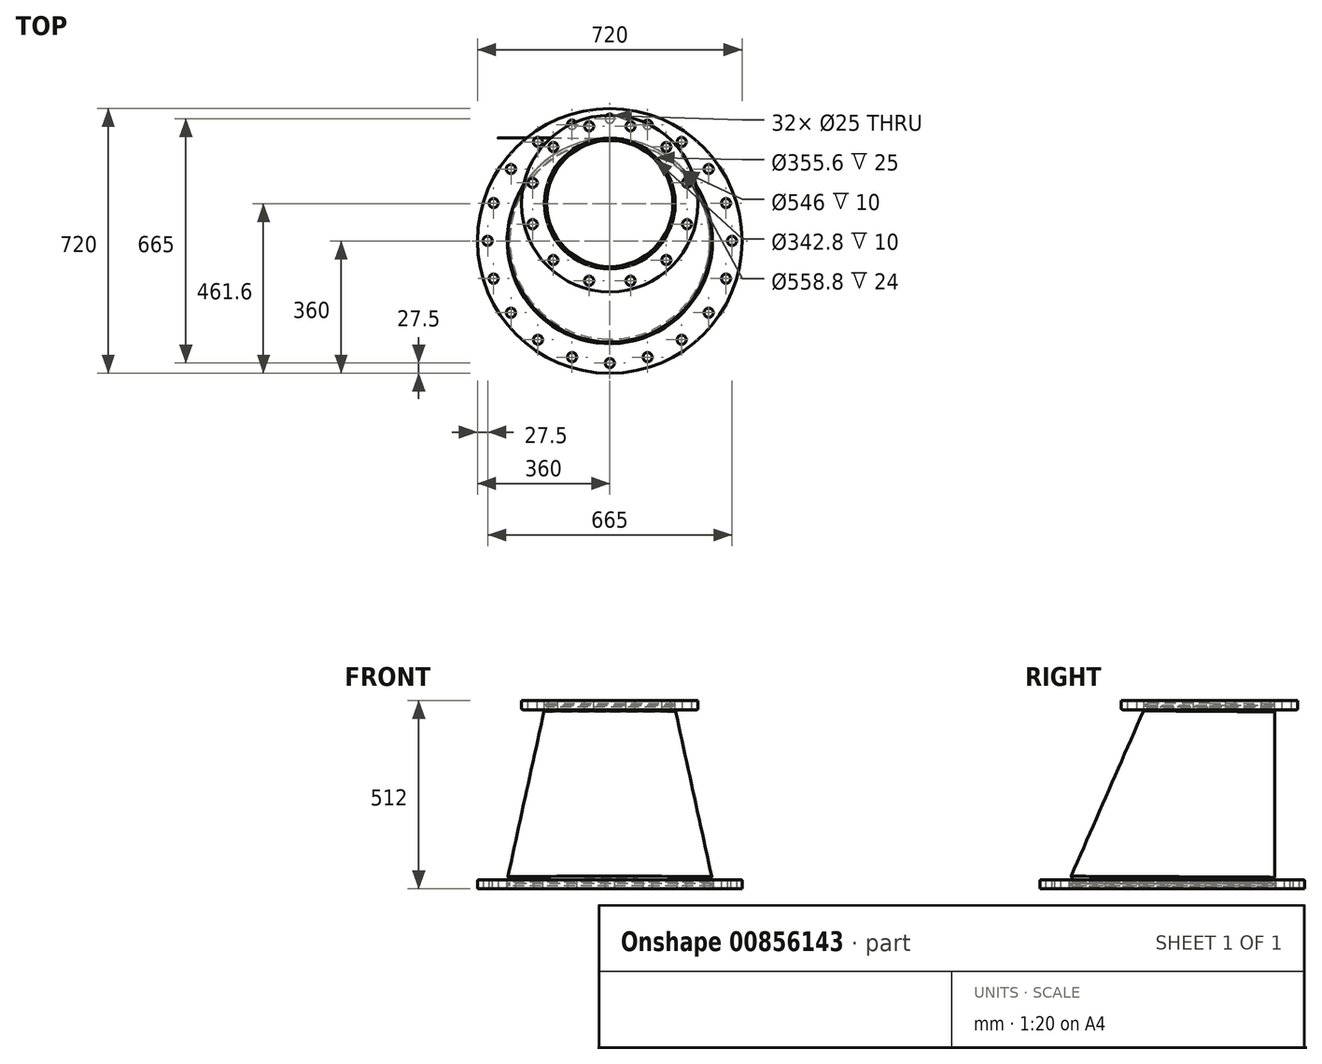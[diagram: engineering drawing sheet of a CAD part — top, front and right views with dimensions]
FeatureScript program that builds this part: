
annotation { "Feature Type Name" : "Feature", "Feature Type Description" : "" }
export const myFeature = defineFeature(function(context is Context, id is Id, definition is map)
    precondition{}
    {
        {
            var Q0;
            Q0=qCreatedBy(makeId("Top.planeOp"),FACE);
            var sketch = newSketch(context, id + "F0", { "sketchPlane" : qUnion([Q0])});
            skCircle(sketch, "E0", {"center": v(0, 0) * mm, "radius": 360 * mm});
            skLineSegment(sketch, "E1", {"start": v(423.48, 0) * mm, "end": v(-426.4, 0) * mm, "construction": true});
            skLineSegment(sketch, "E2", {"start": v(0, 375.02) * mm, "end": v(0, -391.8) * mm, "construction": true});
            skCircle(sketch, "E3", {"center": v(195.44, 269) * mm, "radius": 12.5 * mm});
            skCircle(sketch, "E4.1.0", {"center": v(102.75, 316.23) * mm, "radius": 12.5 * mm});
            skCircle(sketch, "E4.2.0", {"center": v(0, 332.5) * mm, "radius": 12.5 * mm});
            skCircle(sketch, "E4.3.0", {"center": v(-102.75, 316.23) * mm, "radius": 12.5 * mm});
            skCircle(sketch, "E4.4.0", {"center": v(-195.44, 269) * mm, "radius": 12.5 * mm});
            skCircle(sketch, "E4.5.0", {"center": v(-269, 195.44) * mm, "radius": 12.5 * mm});
            skCircle(sketch, "E4.6.0", {"center": v(-316.23, 102.75) * mm, "radius": 12.5 * mm});
            skCircle(sketch, "E4.7.0", {"center": v(-332.5, 0) * mm, "radius": 12.5 * mm});
            skCircle(sketch, "E4.8.0", {"center": v(-316.23, -102.75) * mm, "radius": 12.5 * mm});
            skCircle(sketch, "E4.9.0", {"center": v(-269, -195.44) * mm, "radius": 12.5 * mm});
            skCircle(sketch, "E4.10.0", {"center": v(-195.44, -269) * mm, "radius": 12.5 * mm});
            skCircle(sketch, "E4.11.0", {"center": v(-102.75, -316.23) * mm, "radius": 12.5 * mm});
            skCircle(sketch, "E4.12.0", {"center": v(0, -332.5) * mm, "radius": 12.5 * mm});
            skCircle(sketch, "E4.13.0", {"center": v(102.75, -316.23) * mm, "radius": 12.5 * mm});
            skCircle(sketch, "E4.14.0", {"center": v(195.44, -269) * mm, "radius": 12.5 * mm});
            skCircle(sketch, "E4.15.0", {"center": v(269, -195.44) * mm, "radius": 12.5 * mm});
            skCircle(sketch, "E4.16.0", {"center": v(316.23, -102.75) * mm, "radius": 12.5 * mm});
            skCircle(sketch, "E4.17.0", {"center": v(332.5, 0) * mm, "radius": 12.5 * mm});
            skCircle(sketch, "E4.18.0", {"center": v(316.23, 102.75) * mm, "radius": 12.5 * mm});
            skCircle(sketch, "E4.19.0", {"center": v(269, 195.44) * mm, "radius": 12.5 * mm});
            skCircle(sketch, "E5", {"center": v(0, 0) * mm, "radius": 279.4 * mm});
            skCircle(sketch, "E6", {"center": v(0, 0) * mm, "radius": 332.5 * mm, "construction": true});
            skSolve(sketch);
        }
        {
            var Q0;
            Q0=makeQuery(id+"F0.imprint","IMPRINT",FACE,{"disambiguationData":[TD([[makeQuery(id+"F0.imprint","IMPRINT",EDGE,{"derivedFrom":sQuery(id+"F0.wireOp",EDGE,"E0")}),1.0]])]});
            extrude(context, id + "F1", {"entities" : qUnion([Q0]), "depth" : 24 * mm, "offsetDistance" : 25 * mm});
        }
        {
            var Q0;
            Q0=makeQuery(id+"F1.opExtrude","CAP_EDGE",EDGE,{"disambiguationData":[OSD([sQuery(id+"F0.wireOp",EDGE,"E0")])],"isStart":false});
            fillet(context, id + "F2", {"entities" : qUnion([Q0]), "radius" : 3 * mm, "tangentPropagation" : true, "allowEdgeOverflow" : false});
        }
        {
            var Q0;
            Q0=qCreatedBy(makeId("Top.planeOp"),FACE);
            cPlane(context, id + "F3", {"entities" : qUnion([Q0]), "cplaneType" : CPlaneType.OFFSET, "offset" : 512 * mm, "width" : 150 * mm, "height" : 150 * mm});
        }
        {
            var Q0;
            Q0=qCreatedBy(id+"F3.planeOp",FACE);
            var sketch = newSketch(context, id + "F4", { "sketchPlane" : qUnion([Q0])});
            skCircle(sketch, "E7", {"center": v(0, 101.6) * mm, "radius": 240 * mm});
            skLineSegment(sketch, "E8", {"start": v(0, 382.52) * mm, "end": v(0, -185.4) * mm, "construction": true});
            skLineSegment(sketch, "E9", {"start": v(268.79, 101.6) * mm, "end": v(-280.92, 101.6) * mm, "construction": true});
            skCircle(sketch, "E10", {"center": v(0, 101.6) * mm, "radius": 177.8 * mm});
            skCircle(sketch, "E11", {"center": v(0, 101.6) * mm, "radius": 217.5 * mm, "construction": true});
            skCircle(sketch, "E12", {"center": v(210.09, 157.9) * mm, "radius": 12.5 * mm});
            skCircle(sketch, "E13.1.0", {"center": v(153.8, 255.4) * mm, "radius": 12.5 * mm});
            skCircle(sketch, "E13.2.0", {"center": v(56.3, 311.69) * mm, "radius": 12.5 * mm});
            skCircle(sketch, "E13.3.0", {"center": v(-56.3, 311.69) * mm, "radius": 12.5 * mm});
            skCircle(sketch, "E13.4.0", {"center": v(-153.8, 255.4) * mm, "radius": 12.5 * mm});
            skCircle(sketch, "E13.5.0", {"center": v(-210.09, 157.9) * mm, "radius": 12.5 * mm});
            skCircle(sketch, "E13.6.0", {"center": v(-210.09, 45.3) * mm, "radius": 12.5 * mm});
            skCircle(sketch, "E13.7.0", {"center": v(-153.8, -52.2) * mm, "radius": 12.5 * mm});
            skCircle(sketch, "E13.8.0", {"center": v(-56.3, -108.49) * mm, "radius": 12.5 * mm});
            skCircle(sketch, "E13.9.0", {"center": v(56.3, -108.49) * mm, "radius": 12.5 * mm});
            skCircle(sketch, "E13.10.0", {"center": v(153.8, -52.2) * mm, "radius": 12.5 * mm});
            skCircle(sketch, "E13.11.0", {"center": v(210.09, 45.3) * mm, "radius": 12.5 * mm});
            skSolve(sketch);
        }
        {
            var Q0;
            Q0=makeQuery(id+"F4.imprint","IMPRINT",FACE,{"disambiguationData":[TD([[makeQuery(id+"F4.imprint","IMPRINT",EDGE,{"derivedFrom":sQuery(id+"F4.wireOp",EDGE,"E7")}),1.0]])]});
            extrude(context, id + "F5", {"entities" : qUnion([Q0]), "oppositeDirection" : true, "depth" : 25 * mm, "offsetDistance" : 25 * mm});
        }
        {
            var Q0;
            Q0=makeQuery(id+"F5.opExtrude","CAP_EDGE",EDGE,{"disambiguationData":[OSD([sQuery(id+"F4.wireOp",EDGE,"E7")])],"isStart":false});
            fillet(context, id + "F6", {"entities" : qUnion([Q0]), "radius" : 3 * mm, "tangentPropagation" : true, "allowEdgeOverflow" : false});
        }
        {
            var Q0;
            Q0=qCreatedBy(id+"F3.planeOp",FACE);
            cPlane(context, id + "F7", {"entities" : qUnion([Q0]), "cplaneType" : CPlaneType.OFFSET, "offset" : 7 * mm, "oppositeDirection" : true, "width" : 150 * mm, "height" : 150 * mm});
        }
        {
            var Q0;
            Q0=qCreatedBy(id+"F7.planeOp",FACE);
            var sketch = newSketch(context, id + "F8", { "sketchPlane" : qUnion([Q0])});
            skCircle(sketch, "E14", {"center": v(0, 101.6) * mm, "radius": 177.8 * mm});
            skSolve(sketch);
        }
        {
            var Q0;
            Q0 = qSketchRegion(id + "F8", true);
            extrude(context, id + "F9", {"entities" : qUnion([Q0]), "oppositeDirection" : true, "depth" : 17 * mm, "offsetDistance" : 25 * mm});
        }
        {
            var Q0;
            Q0=qCreatedBy(makeId("Top.planeOp"),FACE);
            cPlane(context, id + "F10", {"entities" : qUnion([Q0]), "cplaneType" : CPlaneType.OFFSET, "offset" : 7 * mm, "width" : 150 * mm, "height" : 150 * mm});
        }
        {
            var Q0;
            Q0=qCreatedBy(id+"F10.planeOp",FACE);
            var sketch = newSketch(context, id + "F11", { "sketchPlane" : qUnion([Q0])});
            skCircle(sketch, "E15", {"center": v(0, 0) * mm, "radius": 279.4 * mm});
            skSolve(sketch);
        }
        {
            var Q0;
            Q0 = qSketchRegion(id + "F11", true);
            extrude(context, id + "F12", {"entities" : qUnion([Q0]), "depth" : 17 * mm, "offsetDistance" : 25 * mm});
        }
        {
            var Q0;
            Q0=makeQuery(id+"F12.opExtrude","CAP_FACE",FACE,{"disambiguationData":[OSD([sQuery(id+"F11.wireOp",EDGE,"E15")])],"isStart":false});
            var sketch = newSketch(context, id + "F13", { "sketchPlane" : qUnion([Q0])});
            skArc(sketch, "E16", {"start": v(4.9, 279.36) * mm, "mid": v(-194.18, 200.9) * mm, "end": v(-279.36, 4.59) * mm});
            skArc(sketch, "E17", {"start": v(279.4, -0.83) * mm, "mid": v(199.58, 195.53) * mm, "end": v(4.9, 279.36) * mm});
            skArc(sketch, "E18", {"start": v(-4.3, -279.37) * mm, "mid": v(195.74, -199.37) * mm, "end": v(279.4, -0.83) * mm});
            skArc(sketch, "E19", {"start": v(-279.36, 4.59) * mm, "mid": v(-200.68, -194.4) * mm, "end": v(-4.3, -279.37) * mm});
            skSolve(sketch);
        }
        {
            var Q0;
            Q0=makeQuery(id+"F9.opExtrude","CAP_FACE",FACE,{"disambiguationData":[OSD([sQuery(id+"F8.wireOp",EDGE,"E14")])],"isStart":false});
            var sketch = newSketch(context, id + "F14", { "sketchPlane" : qUnion([Q0])});
            skArc(sketch, "E20", {"start": v(0.67, 76.2) * mm, "mid": v(-125.72, 24.12) * mm, "end": v(-177.8, -102.26) * mm});
            skArc(sketch, "E21", {"start": v(177.7, -107.31) * mm, "mid": v(127.96, 21.85) * mm, "end": v(0.67, 76.2) * mm});
            skArc(sketch, "E22", {"start": v(-0.66, -279.4) * mm, "mid": v(123.45, -229.56) * mm, "end": v(177.7, -107.31) * mm});
            skArc(sketch, "E23", {"start": v(-177.8, -102.26) * mm, "mid": v(-125.72, -227.33) * mm, "end": v(-0.66, -279.4) * mm});
            skSolve(sketch);
        }
        {
            var Q0;
            Q0 = qSketchRegion(id + "F13", true);
            var Q1;
            Q1 = qSketchRegion(id + "F14", true);
            loft(context, id + "F15", {"sheetProfilesArray" : [{ "sheetProfileEntities" : qUnion([Q0]) }, { "sheetProfileEntities" : qUnion([Q1]) }]});
        }
        {
            var Q0;
            Q0=makeQuery(id+"F12.opExtrude","CAP_FACE",FACE,{"disambiguationData":[OSD([sQuery(id+"F11.wireOp",EDGE,"E15")])],"isStart":true});
            var Q1;
            Q1=makeQuery(id+"F9.opExtrude","CAP_FACE",FACE,{"disambiguationData":[OSD([sQuery(id+"F8.wireOp",EDGE,"E14")])],"isStart":true});
            shell(context, id + "F16", {"entities" : qUnion([Q0, Q1]), "thickness" : 6.4 * mm});
        }
        {
            var Q0;
            Q0=makeQuery(id+"F9.opExtrude","CAP_EDGE",EDGE,{"disambiguationData":[OSD([sQuery(id+"F8.wireOp",EDGE,"E14")])],"isStart":true});
            var Q1;
            Q1=makeQuery(id+"F12.opExtrude","CAP_EDGE",EDGE,{"disambiguationData":[OSD([sQuery(id+"F11.wireOp",EDGE,"E15")])],"isStart":true});
            chamfer(context, id + "F17", {"entities" : qUnion([Q0, Q1]), "width" : 7 * mm, "tangentPropagation" : true});
        }
        {
            var Q0;
            Q0=makeQuery(id+"F15.opLoft","SWEPT_FACE",FACE,{"disambiguationData":[OSD([sQuery(id+"F13.wireOp",EDGE,"E16"),sQuery(id+"F13.wireOp",EDGE,"E17"),sQuery(id+"F13.wireOp",EDGE,"E19"),sQuery(id+"F14.wireOp",EDGE,"E20"),sQuery(id+"F14.wireOp",EDGE,"E22"),sQuery(id+"F14.wireOp",EDGE,"E23")])]});
            chamfer(context, id + "F18", {"entities" : qUnion([Q0]), "width" : 7 * mm, "tangentPropagation" : true});
        }
    });
